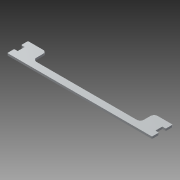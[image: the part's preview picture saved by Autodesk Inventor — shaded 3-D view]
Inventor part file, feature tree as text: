
AUTODESK INVENTOR PART (.ipt)
format: ipt  version: 2013 (Build 170138000, 138)  size: 129,024 bytes
history: native  units: mm
features: extrude x1, sketch x1
ambient origin geometry x8: Origin, YZ Plane, XZ Plane, XY Plane, X Axis, Y Axis, Z Axis, Center Point
bodies: Solid1 (feature_tree)
feature tree (2):
  extrude  "Extrusion1"  Depth=1.0mm
  sketch  "Sketch1"  dims[d0=10.0mm d2=1.0mm d3=3.0mm d4=0.0mm d8=27.0mm d9=10.0mm d10=5.0mm d11=5.0mm d12=1.0mm d13=27.0mm d14=5.0mm d15=10.0mm d16=10.0mm d17=30.0mm d18=1.0mm d19=30.0mm d20=210.0mm d21=5.0mm]
